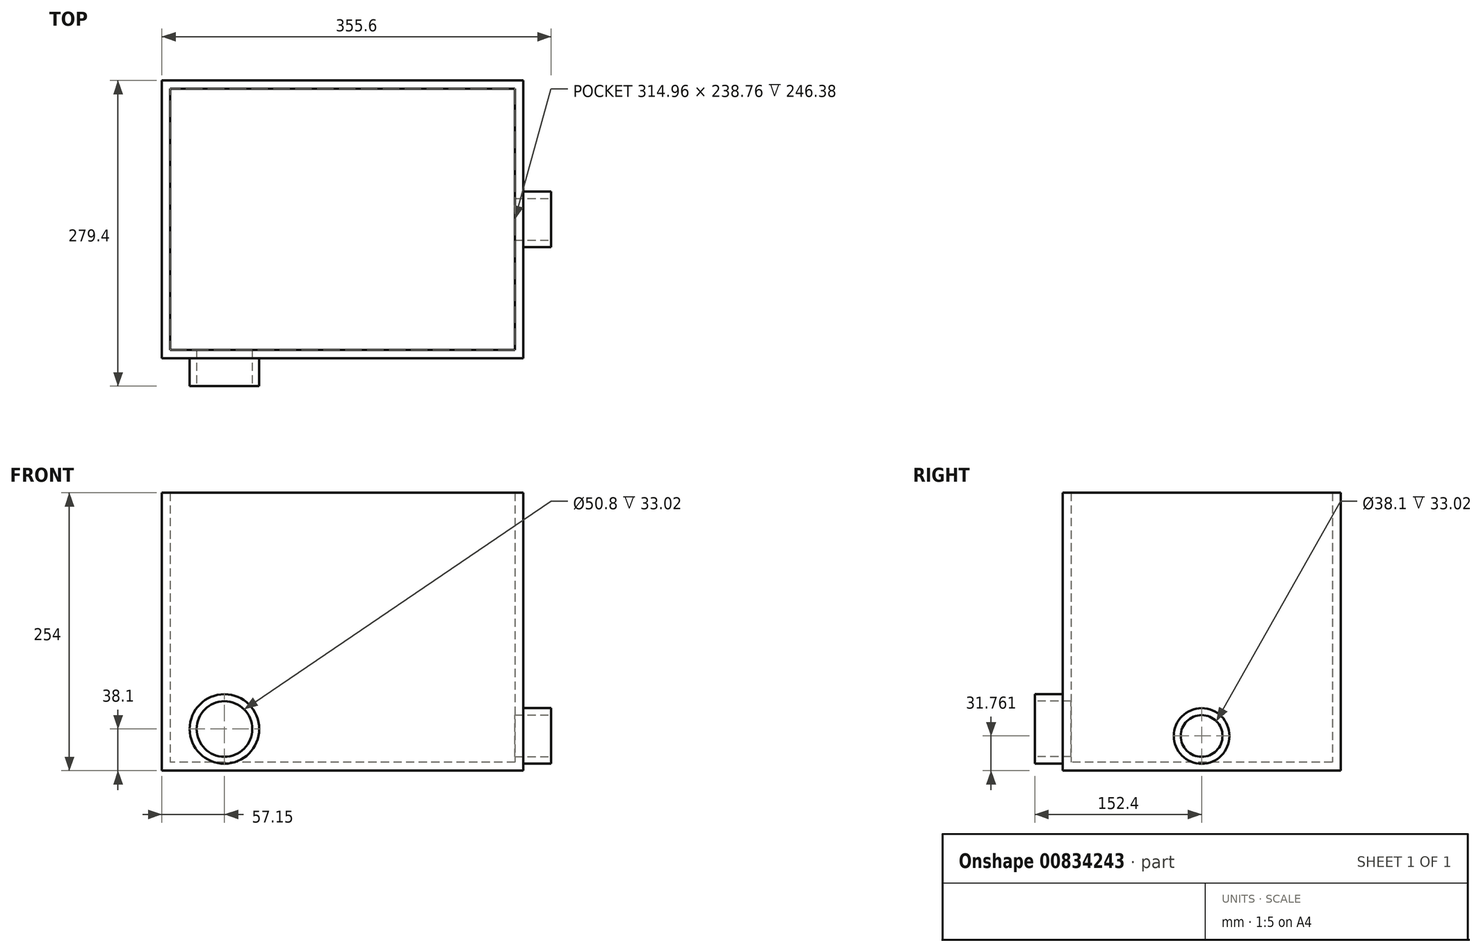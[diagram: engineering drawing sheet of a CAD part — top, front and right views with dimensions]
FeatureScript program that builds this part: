
annotation { "Feature Type Name" : "Feature", "Feature Type Description" : "" }
export const myFeature = defineFeature(function(context is Context, id is Id, definition is map)
    precondition{}
    {
        {
            var Q0;
            Q0=qCreatedBy(makeId("Top.planeOp"),FACE);
            var sketch = newSketch(context, id + "F0", { "sketchPlane" : qUnion([Q0])});
            skLineSegment(sketch, "E0.bottom", {"start": v(165.1, 127) * mm, "end": v(-165.1, 127) * mm});
            skLineSegment(sketch, "E0.top", {"start": v(165.1, -127) * mm, "end": v(-165.1, -127) * mm});
            skLineSegment(sketch, "E0.left", {"start": v(165.1, 127) * mm, "end": v(165.1, -127) * mm});
            skLineSegment(sketch, "E0.right", {"start": v(-165.1, 127) * mm, "end": v(-165.1, -127) * mm});
            skPoint(sketch, "E0.middle", {"position": v(0, 0) * mm});
            skSolve(sketch);
        }
        {
            var Q0;
            Q0=makeQuery(id+"F0.imprint","IMPRINT",FACE,{"disambiguationData":[TD([[makeQuery(id+"F0.imprint","IMPRINT",EDGE,{"derivedFrom":sQuery(id+"F0.wireOp",EDGE,"E0.bottom")}),1.0]])]});
            extrude(context, id + "F1", {"entities" : qUnion([Q0]), "depth" : 254 * mm, "offsetDistance" : 25.4 * mm});
        }
        {
            var Q0;
            Q0=makeQuery(id+"F1.opExtrude","CAP_FACE",FACE,{"disambiguationData":[OSD([sQuery(id+"F0.wireOp",EDGE,"E0.bottom"),sQuery(id+"F0.wireOp",EDGE,"E0.top"),sQuery(id+"F0.wireOp",EDGE,"E0.left"),sQuery(id+"F0.wireOp",EDGE,"E0.right")])],"isStart":false});
            shell(context, id + "F2", {"entities" : qUnion([Q0]), "thickness" : 7.62 * mm});
        }
        {
            var Q0;
            Q0=makeQuery(id+"F1.opExtrude","SWEPT_FACE",FACE,{"disambiguationData":[OSD([sQuery(id+"F0.wireOp",EDGE,"E0.left")])]});
            var sketch = newSketch(context, id + "F3", { "sketchPlane" : qUnion([Q0])});
            skCircle(sketch, "E1", {"center": v(0, 31.76) * mm, "radius": 25.4 * mm});
            skSolve(sketch);
        }
        {
            var Q0;
            Q0=makeQuery(id+"F3.imprint","IMPRINT",FACE,{"disambiguationData":[TD([[makeQuery(id+"F3.imprint","IMPRINT",EDGE,{"derivedFrom":sQuery(id+"F3.wireOp",EDGE,"E1")}),1.0]])]});
            var Q1;
            Q1=sQuery(id+"F3.wireOp",EDGE,"E1");
            extrude(context, id + "F4", {"entities" : qUnion([Q0]), "operationType" : NewBodyOperationType.ADD, "surfaceEntities" : qUnion([Q1]), "depth" : 25.4 * mm, "offsetDistance" : 25.4 * mm});
        }
        {
            var Q0;
            Q0=makeQuery(id+"F4.opExtrude","CAP_FACE",FACE,{"disambiguationData":[OSD([sQuery(id+"F3.wireOp",EDGE,"E1")])],"isStart":false});
            var sketch = newSketch(context, id + "F5", { "sketchPlane" : qUnion([Q0])});
            skCircle(sketch, "E2", {"center": v(0, 31.76) * mm, "radius": 19.05 * mm});
            skSolve(sketch);
        }
        {
            var Q0;
            Q0=sQuery(id+"F5.wireOp",VERTEX,"E2.center");
            var Q1;
            Q1=makeQuery(id+"F1.opExtrude","SWEPT_BODY",BODY,{"disambiguationData":[OSD([sQuery(id+"F0.wireOp",EDGE,"E0.bottom"),sQuery(id+"F0.wireOp",EDGE,"E0.top"),sQuery(id+"F0.wireOp",EDGE,"E0.left"),sQuery(id+"F0.wireOp",EDGE,"E0.right")])]});
            var Q2;
            Q2=makeQuery(id+"F4.opExtrude","SWEPT_BODY",BODY,{"disambiguationData":[OSD([sQuery(id+"F3.wireOp",EDGE,"E1")])]});
            hole(context, id + "F6", {"style" : HoleStyle.SIMPLE, "endStyle" : HoleEndStyle.BLIND, "holeDiameter" : 38.1 * mm, "majorDiameter" : 6.35 * mm, "holeDepth" : 76.2 * mm, "isTappedThrough" : true, "tappedDepth" : 12.7 * mm, "tapClearance" : 3, "locations" : qUnion([Q0]), "scope" : qUnion([Q1, Q2])});
        }
        {
            var Q0;
            Q0=makeQuery(id+"F1.opExtrude","SWEPT_FACE",FACE,{"disambiguationData":[OSD([sQuery(id+"F0.wireOp",EDGE,"E0.top")])]});
            var sketch = newSketch(context, id + "F7", { "sketchPlane" : qUnion([Q0])});
            skCircle(sketch, "E3", {"center": v(-107.95, 38.1) * mm, "radius": 31.75 * mm});
            skSolve(sketch);
        }
        {
            var Q0;
            Q0=makeQuery(id+"F7.imprint","IMPRINT",FACE,{"disambiguationData":[TD([[makeQuery(id+"F7.imprint","IMPRINT",EDGE,{"derivedFrom":sQuery(id+"F7.wireOp",EDGE,"E3")}),1.0]])]});
            var Q1;
            Q1=sQuery(id+"F7.wireOp",EDGE,"E3");
            extrude(context, id + "F8", {"entities" : qUnion([Q0]), "operationType" : NewBodyOperationType.ADD, "surfaceEntities" : qUnion([Q1]), "depth" : 25.4 * mm, "offsetDistance" : 25.4 * mm});
        }
        {
            var Q0;
            Q0=makeQuery(id+"F8.opExtrude","CAP_FACE",FACE,{"disambiguationData":[OSD([sQuery(id+"F7.wireOp",EDGE,"E3")])],"isStart":false});
            var sketch = newSketch(context, id + "F9", { "sketchPlane" : qUnion([Q0])});
            skCircle(sketch, "E4", {"center": v(-107.95, 38.1) * mm, "radius": 25.4 * mm});
            skSolve(sketch);
        }
        {
            var Q0;
            Q0=makeQuery(id+"F9.imprint","IMPRINT",FACE,{"disambiguationData":[TD([[makeQuery(id+"F9.imprint","IMPRINT",EDGE,{"derivedFrom":sQuery(id+"F9.wireOp",EDGE,"E4")}),1.0]])]});
            extrude(context, id + "F10", {"entities" : qUnion([Q0]), "operationType" : NewBodyOperationType.REMOVE, "oppositeDirection" : true, "depth" : 76.2 * mm, "offsetDistance" : 25.4 * mm});
        }
    });
